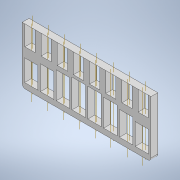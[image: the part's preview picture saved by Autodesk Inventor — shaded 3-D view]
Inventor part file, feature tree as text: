
AUTODESK INVENTOR PART (.ipt)
format: ipt  version: 2022 (Build 260153000, 153)  size: 300,544 bytes
history: native  units: mm
features: other x16, projected_geometry x16, sketch x5, extrude x3, pattern_linear x1, plane x1, mirror x1, chamfer x1, fillet x1
ambient origin geometry x8: Origin, YZ Plane, XZ Plane, XY Plane, X Axis, Y Axis, Z Axis, Center Point
bodies: Solid1 (feature_tree)
feature tree (45):
  extrude  "Extrusion1"  Depth=105.0mm
  extrude  "Extrusion2"  Depth=19.0mm
  pattern_linear  "Rectangular Pattern2"  Spacing1=12.7mm  [1 undecoded]
  extrude  "Extrusion3"  Depth=211.0mm
  plane  "Work Plane1"
  mirror  "Mirror1"
  sketch  "Sketch4"  dims[d26=5.0mm]
  other  "Work Axis1"
  other  "Work Axis2"
  other  "Work Axis3"
  other  "Work Axis4"
  other  "Work Axis5"
  other  "Work Axis6"
  other  "Work Axis15"
  other  "Work Axis16"
  sketch  "Sketch5"  dims[d27=5.0mm d28=12.7mm d29=0.0mm d30=80.0mm d32=211.0mm d33=25.0mm d34=48.0mm d37=35.0mm d38=40.0mm d39=45.0mm d41=2.222222mm d42=4.444444mm d43=4.444444mm d44=4.444444mm d45=4.444444mm d46=12.7mm d47=0.0mm d48=8.5mm d49=11.5mm d50=5.0mm d51=2.0mm d52=45.0deg d53=10.0mm d54=6.0mm]
  other  "Work Axis7"
  other  "Work Axis8"
  other  "Work Axis9"
  other  "Work Axis10"
  other  "Work Axis11"
  other  "Work Axis12"
  other  "Work Axis13"
  other  "Work Axis14"
  chamfer  "Chamfer1"  Distance=25.0mm
  fillet  "Fillet1"  Radius=48.0mm
  sketch  "Sketch1"  dims[d0=240.0mm d1=105.0mm]
  sketch  "Sketch2"  dims[d2=12.7mm d3=0.0mm d24=19.0mm]
  sketch  "Sketch3"  dims[d25=32.0mm]
  projected_geometry  "Projected Loop1"
  projected_geometry  "Projected Loop2"
  projected_geometry  "Projected Loop3"
  projected_geometry  "Projected Loop4"
  projected_geometry  "Projected Loop5"
  projected_geometry  "Projected Loop6"
  projected_geometry  "Projected Loop7"
  projected_geometry  "Projected Loop8"
  projected_geometry  "Projected Loop9"
  projected_geometry  "Projected Loop10"
  projected_geometry  "Projected Loop11"
  projected_geometry  "Projected Loop12"
  projected_geometry  "Projected Loop13"
  projected_geometry  "Projected Loop14"
  projected_geometry  "Projected Loop15"
  projected_geometry  "Projected Loop16"
note: 1 required parameter value undecoded (feature->parameter linkage not recoverable at this tier; creation-order binding heuristic only, values carry confidence <= 0.55)
